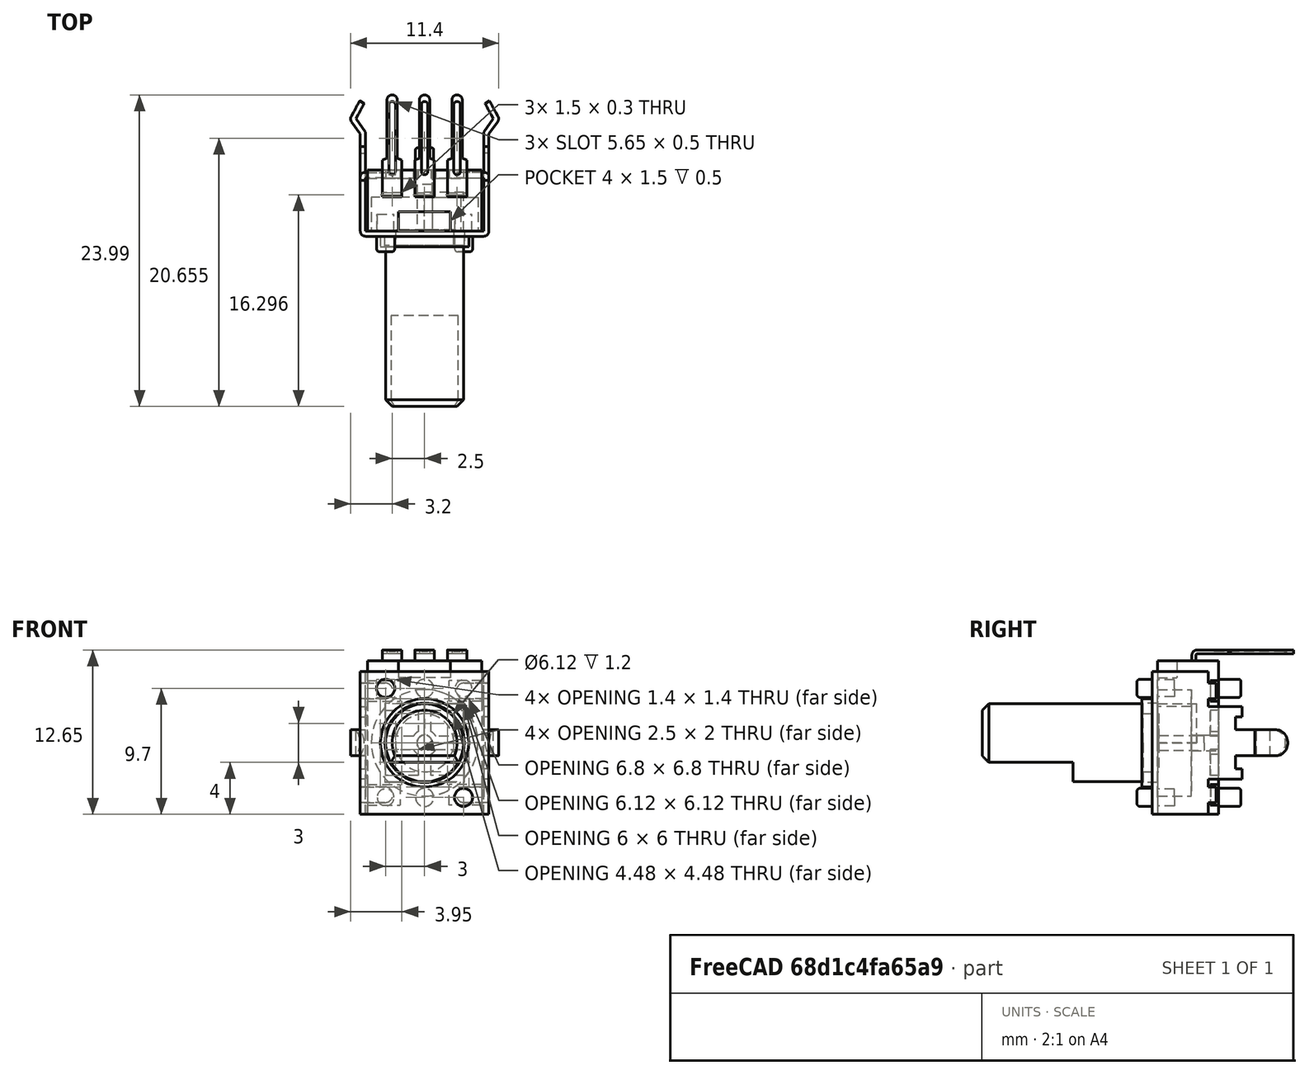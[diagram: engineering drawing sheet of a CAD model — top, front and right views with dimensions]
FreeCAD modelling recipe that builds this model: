
FCSTD DOCUMENT  (FreeCAD 1.0R38641 +468 (Git))
Label: THT-POT
License: All rights reserved
LicenseURL: https://en.wikipedia.org/wiki/All_rights_reserved
objects: Part::Feature×2, PartDesign::Body×2, PartDesign::AdditiveBox×1, PartDesign::Boolean×1
note: 9 computed .brp shape members not serialized (recipe doc carries the construction recipe); baked Part::Feature solids carry a one-line shape summary decoded from their .brp

FEATURE [Part::Feature] Part__Feature  label="PTV09A-4X20F-XXXCX"
  shape: bbox 11.4 x 12.09 x 12.65 mm, 219 faces (baked)
FEATURE [Part::Feature] Part__Feature001  label="PTV09A-4X20F-XXXCX001"
  shape: bbox 6.1 x 17.1 x 6.1 mm, 17 faces (baked)
FEATURE [PartDesign::AdditiveBox] Box
  AttacherType = Attacher::AttachEngine3D
  Height = 3
  Length = 3
  Refine = true
  Suppressed = false
  Width = 3
FEATURE [PartDesign::Body] Body001  label="Glue"
  AllowCompound = false
  Group = -> [Box]
  Origin = -> Origin001
  Tip = -> Box
FEATURE [PartDesign::Boolean] Boolean
  Group = -> [Part__Feature,Part__Feature001,Body001]
  Refine = true
  Suppressed = false
  Type = 0
  UsePlacement = true
FEATURE [PartDesign::Body] Body  label="THT-POT"
  AllowCompound = false
  Group = -> [Boolean]
  Origin = -> Origin
  Tip = -> Boolean
